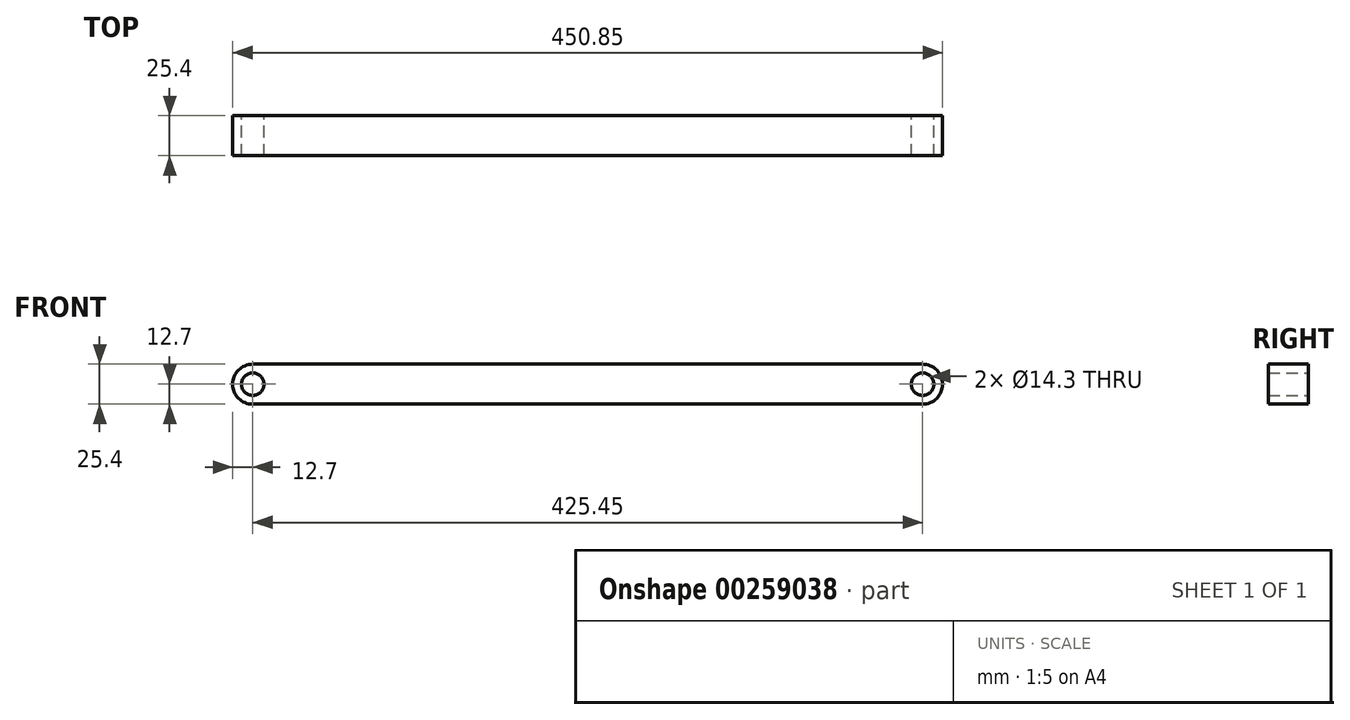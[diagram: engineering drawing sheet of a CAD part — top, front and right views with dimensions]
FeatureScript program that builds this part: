
annotation { "Feature Type Name" : "Feature", "Feature Type Description" : "" }
export const myFeature = defineFeature(function(context is Context, id is Id, definition is map)
    precondition{}
    {
        {
            var Q0;
            Q0=qCreatedBy(makeId("Front.planeOp"),FACE);
            var sketch = newSketch(context, id + "F0", { "sketchPlane" : qUnion([Q0])});
            skCircle(sketch, "E0", {"center": v(0, 0) * mm, "radius": 12.7 * mm});
            skCircle(sketch, "E1", {"center": v(0, 0) * mm, "radius": 7.15 * mm});
            skCircle(sketch, "E2", {"center": v(425.45, 0) * mm, "radius": 12.7 * mm});
            skCircle(sketch, "E3", {"center": v(425.45, 0) * mm, "radius": 7.15 * mm});
            skLineSegment(sketch, "E4", {"start": v(0, 12.7) * mm, "end": v(425.45, 12.7) * mm});
            skLineSegment(sketch, "E5", {"start": v(0, -12.7) * mm, "end": v(425.45, -12.7) * mm});
            skSolve(sketch);
        }
        {
            var Q0;
            {var subQ0=sQuery(id+"F0.wireOp",EDGE,"E4");Q0=makeQuery(id+"F0.imprint","IMPRINT",FACE,{"disambiguationData":[TD([[makeQuery(id+"F0.imprint","IMPRINT",EDGE,{"derivedFrom":subQ0}),-1.0]])]});}
            var Q1;
            Q1=makeQuery(id+"F0.imprint","IMPRINT",FACE,{"disambiguationData":[TD([[makeQuery(id+"F0.imprint","IMPRINT",EDGE,{"derivedFrom":sQuery(id+"F0.wireOp",EDGE,"E1")}),-1.0]])]});
            var Q2;
            Q2=makeQuery(id+"F0.imprint","IMPRINT",FACE,{"disambiguationData":[TD([[makeQuery(id+"F0.imprint","IMPRINT",EDGE,{"derivedFrom":sQuery(id+"F0.wireOp",EDGE,"E3")}),-1.0]])]});
            extrude(context, id + "F1", {"entities" : qUnion([Q0, Q1, Q2]), "depth" : 25.4 * mm});
        }
    });
